# Revit family: RN 90089 Optifitt-Serra-Verschlusskappe
name_source: partatom
category: Rohrformteile
units: mm (PartAtom-declared; Revit-internal decimal feet)

## family parameters
Arbeitsebenenbasiert = Nein
Beim Laden mit Abzugskörper schneiden = Nein
Bemaßung runder Anschluss = Durchmesser verwenden
Gemeinsam genutzt = Nein
Immer vertikal = Ja
Teiletyp = Nicht definiert

## types (6) — shared parameters
1.010.00.2 Blattnummer der Richtlinie = 29
1.010.00.3 Ausgabedatum (Monat) der Richtlinie = 201308
1.010.00.4 Herstellername = R. Nussbaum AG
1.010.00.5 Revisionsdatum der Datei = 20190521
1.010.00.6 Webadresse des Herstellers = http://www.nussbaum.ch
1.100.00.4 Produktbezeichnung = Versorgung
1.110.00.2 Index = 3
1.110.00.4 Produktbezeichnung = Optifitt-Serra
1.960/3L.00.8 Link (URL) = https://www.nussbaum.ch
29.700.00.4 Produktname = Optifitt-Serra-Verschlusskappe
29.700.00.5 Produktkennung = 2
29.700.00.6 Querschnittsform = 1
29.700.00.7 Nennweitensystem = DN
29.700.00.8 Nenndrucksystem = PN
29.710.02.4 Nenndruck = 16
29.710.02.5 max. zul. Überdruck [hPa] = 1600
29.710.02.7 max. zul. Dauer-Betriebsdruck [hPa] = 1600
29.710.02.9 max. zul. Dauer-Betriebstemperatur [°C] = 90
Connector Visibility = Nein
EnclosingSpace Visibility = Nein
Hersteller = R. Nussbaum AG
URL = https://www.nussbaum.ch

## per-type parameters (varying)
| type | 1.800.00.3 TGA-Nummer | 1.800.00.4 Kommentarfeld | 1.810.00.3 Hersteller-Bestellnummer | 1.810.00.4 DATANORM-Nummer | 1.810.00.5 StLB-Nummer | 1.810.00.6 GTIN-Nummer | 29.710.02.10 Formstück-Gewicht [kg] | 29.710.02.3 Benennung | CONNECTOR0_DIAMETER_dX_0r | CONNECTOR0_dX_01 | CONNECTOR0_ref_dX | Modell | R. Nussbaum AG 90089.04 de Visibility | R. Nussbaum AG 90089.05 de Visibility | R. Nussbaum AG 90089.06 de Visibility | R. Nussbaum AG 90089.07 de Visibility | R. Nussbaum AG 90089.08 de Visibility | R. Nussbaum AG 90089.09 de Visibility | Typenkommentare |
| DN=50 | 01900300000000000000000000000000000000000000000023000000000000000014 | 90089.09, Optifitt-Serra-Verschlusskappe, DN=50, L=34 | 90089.09 | 90089.09 | 216.137 | 7612945680648 | 0.507 | Optifitt-Serra-Verschlusskappe, DN=50, L=34 | 50 mm | 24 mm | 24 mm | 90089.09 | Nein | Nein | Nein | Nein | Nein | Ja | Optifitt-Serra-Verschlusskappe  DN=50 |
| DN=40 | 01900300000000000000000000000000000000000000000023000000000000000013 | 90089.08, Optifitt-Serra-Verschlusskappe, DN=40, L=28 | 90089.08 | 90089.08 | 216.136 | 7612945680631 | 0.255 | Optifitt-Serra-Verschlusskappe, DN=40, L=28 | 40 mm | 19 mm | 19 mm | 90089.08 | Nein | Nein | Nein | Nein | Ja | Nein | Optifitt-Serra-Verschlusskappe  DN=40 |
| DN=32 | 01900300000000000000000000000000000000000000000023000000000000000012 | 90089.07, Optifitt-Serra-Verschlusskappe, DN=32, L=28 | 90089.07 | 90089.07 | 216.135 | 7612945680624 | 0.23 | Optifitt-Serra-Verschlusskappe, DN=32, L=28 | 32 mm | 19 mm | 19 mm | 90089.07 | Nein | Nein | Nein | Ja | Nein | Nein | Optifitt-Serra-Verschlusskappe  DN=32 |
| DN=25 | 01900300000000000000000000000000000000000000000023000000000000000011 | 90089.06, Optifitt-Serra-Verschlusskappe, DN=25, L=25 | 90089.06 | 90089.06 | 216.134 | 7612945680617 | 0.116 | Optifitt-Serra-Verschlusskappe, DN=25, L=25 | 25 mm  [stored 0.082021 ft] | 17 mm | 17 mm | 90089.06 | Nein | Nein | Ja | Nein | Nein | Nein | Optifitt-Serra-Verschlusskappe  DN=25 |
| DN=20 | 01900300000000000000000000000000000000000000000023000000000000000010 | 90089.05, Optifitt-Serra-Verschlusskappe, DN=20, L=24 | 90089.05 | 90089.05 | 216.133 | 7612945680600 | 0.069 | Optifitt-Serra-Verschlusskappe, DN=20, L=24 | 20 mm | 15 mm  [stored 0.0492126 ft] | 15 mm  [stored 0.0492126 ft] | 90089.05 | Nein | Ja | Nein | Nein | Nein | Nein | Optifitt-Serra-Verschlusskappe  DN=20 |
| DN=15 | 01900300000000000000000000000000000000000000000023000000000000000009 | 90089.04, Optifitt-Serra-Verschlusskappe, DN=15, L=20 | 90089.04 | 90089.04 | 216.132 | 7612945679994 | 0.07 | Optifitt-Serra-Verschlusskappe, DN=15, L=20 | 15 mm  [stored 0.0492126 ft] | 13 mm | 13 mm | 90089.04 | Ja | Nein | Nein | Nein | Nein | Nein | Optifitt-Serra-Verschlusskappe  DN=15 |

note: [stored X ft] marks values corroborated as IEEE doubles in the binary element streams (Revit-internal decimal feet)

## geometry (parser evidence)
native form markers: Sweep x2
no freeform markers — native parametric forms only
